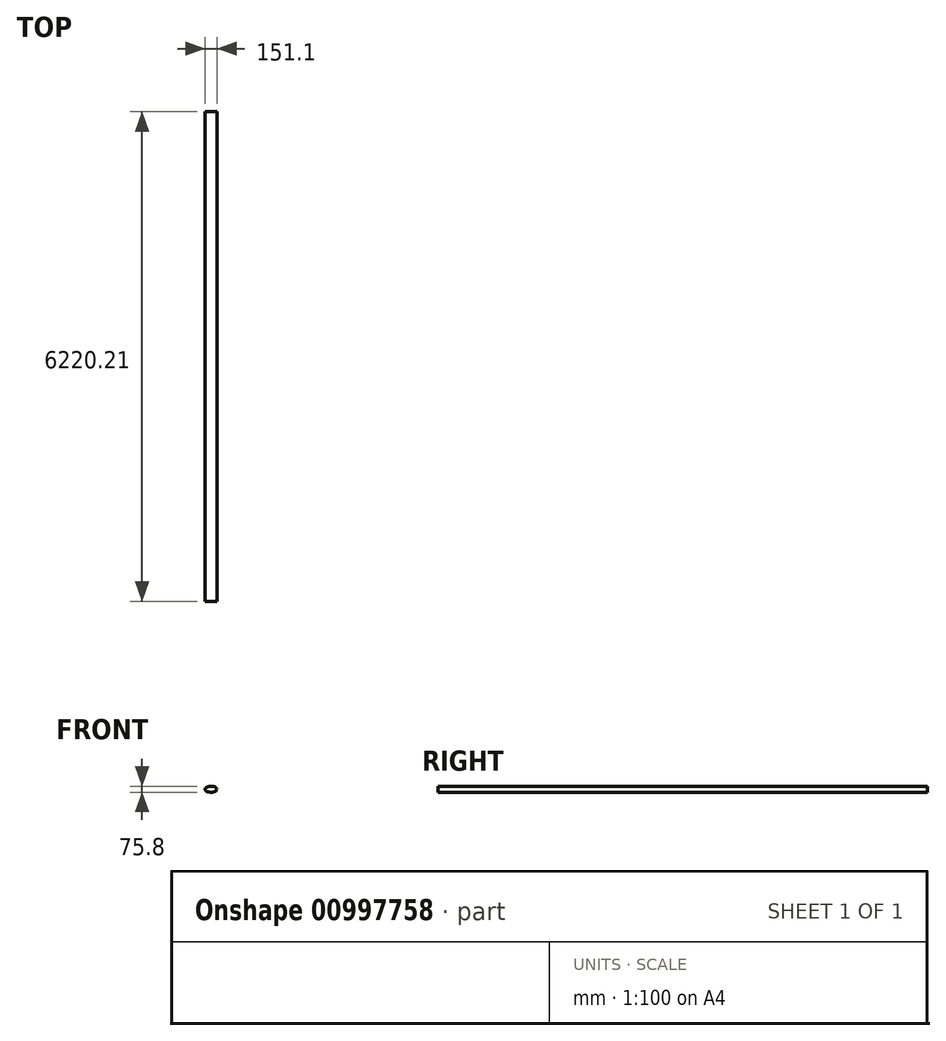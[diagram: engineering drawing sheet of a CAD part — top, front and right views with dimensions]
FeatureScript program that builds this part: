
annotation { "Feature Type Name" : "Feature", "Feature Type Description" : "" }
export const myFeature = defineFeature(function(context is Context, id is Id, definition is map)
    precondition{}
    {
        {
            var Q0;
            Q0=qCreatedBy(makeId("Front.planeOp"),FACE);
            var sketch = newSketch(context, id + "F0", { "sketchPlane" : qUnion([Q0])});
            skEllipse(sketch, "E0", {"center": v(0, 0) * mm, "majorRadius": 75.55 * mm, "minorRadius": 37.9 * mm, "majorAxis": v(1, 0)});
            skSolve(sketch);
        }
        {
            var Q0;
            Q0 = qSketchRegion(id + "F0", true);
            extrude(context, id + "F1", {"entities" : qUnion([Q0]), "oppositeDirection" : true, "depth" : 6220.2 * mm, "offsetDistance" : 25.4 * mm});
        }
    });
